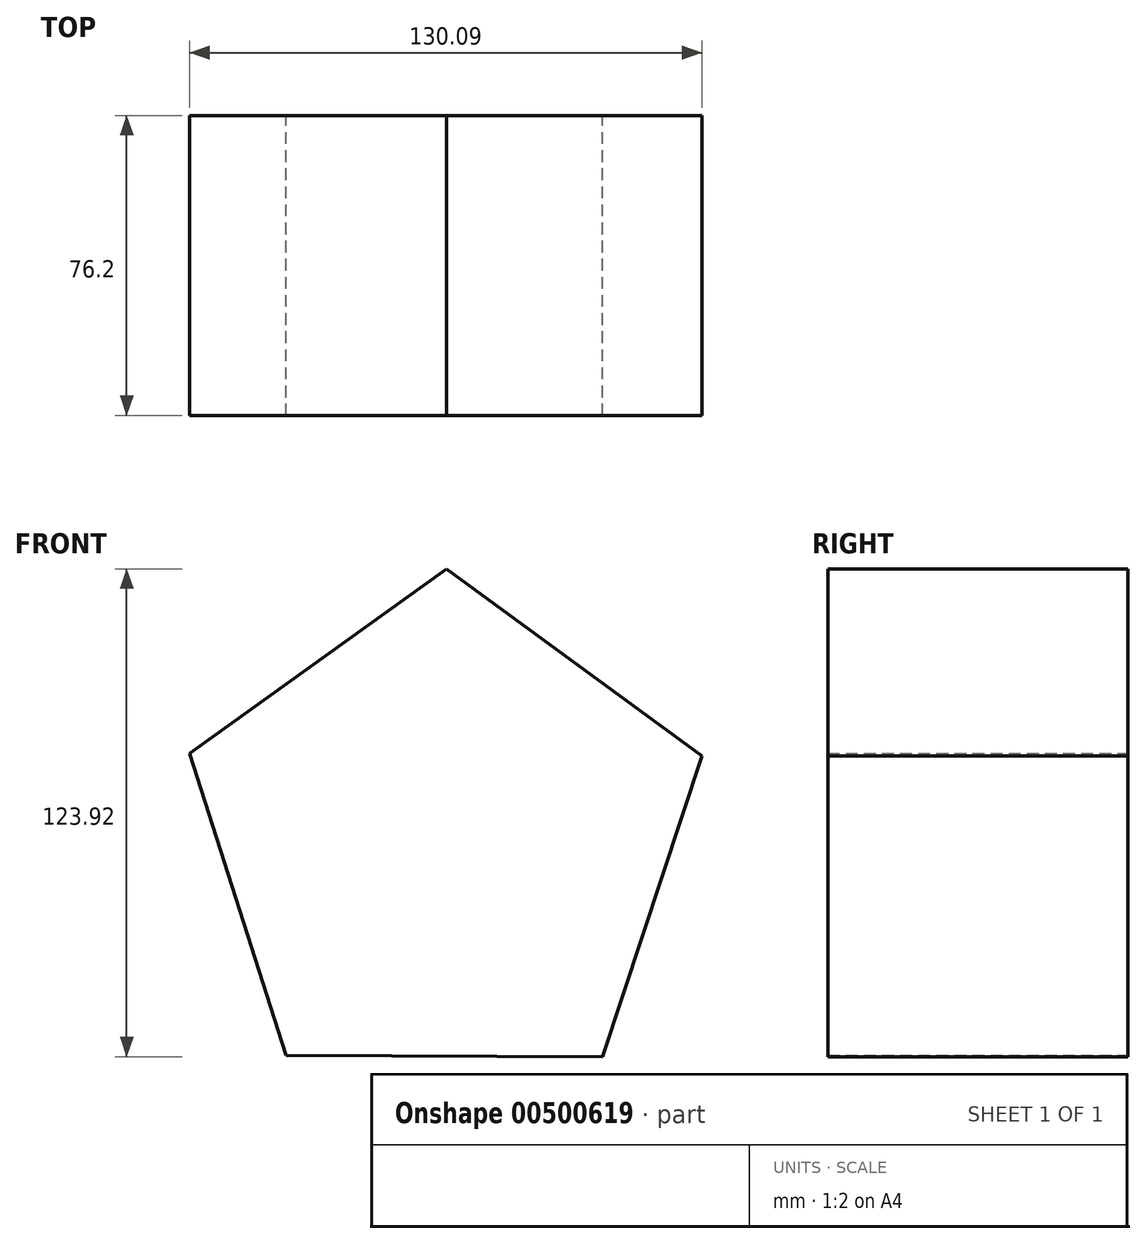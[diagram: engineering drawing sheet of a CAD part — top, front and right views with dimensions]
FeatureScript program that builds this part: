
annotation { "Feature Type Name" : "Feature", "Feature Type Description" : "" }
export const myFeature = defineFeature(function(context is Context, id is Id, definition is map)
    precondition{}
    {
        {
            var Q0;
            Q0=qCreatedBy(makeId("Front.planeOp"),FACE);
            var sketch = newSketch(context, id + "F0", { "sketchPlane" : qUnion([Q0])});
            skCircle(sketch, "E0.cCircle", {"center": v(0, 0) * mm, "radius": 68.4 * mm, "construction": true});
            skLineSegment(sketch, "E0.0", {"start": v(65.15, 20.82) * mm, "end": v(39.93, -55.53) * mm});
            skLineSegment(sketch, "E0.1", {"start": v(39.93, -55.53) * mm, "end": v(-40.47, -55.14) * mm});
            skLineSegment(sketch, "E0.2", {"start": v(-40.47, -55.14) * mm, "end": v(-64.94, 21.45) * mm});
            skLineSegment(sketch, "E0.3", {"start": v(-64.94, 21.45) * mm, "end": v(0.33, 68.4) * mm});
            skLineSegment(sketch, "E0.4", {"start": v(0.33, 68.4) * mm, "end": v(65.15, 20.82) * mm});
            skSolve(sketch);
        }
        {
            var Q0;
            Q0 = qSketchRegion(id + "F0", true);
            extrude(context, id + "F1", {"entities" : qUnion([Q0]), "depth" : 76.2 * mm});
        }
    });
